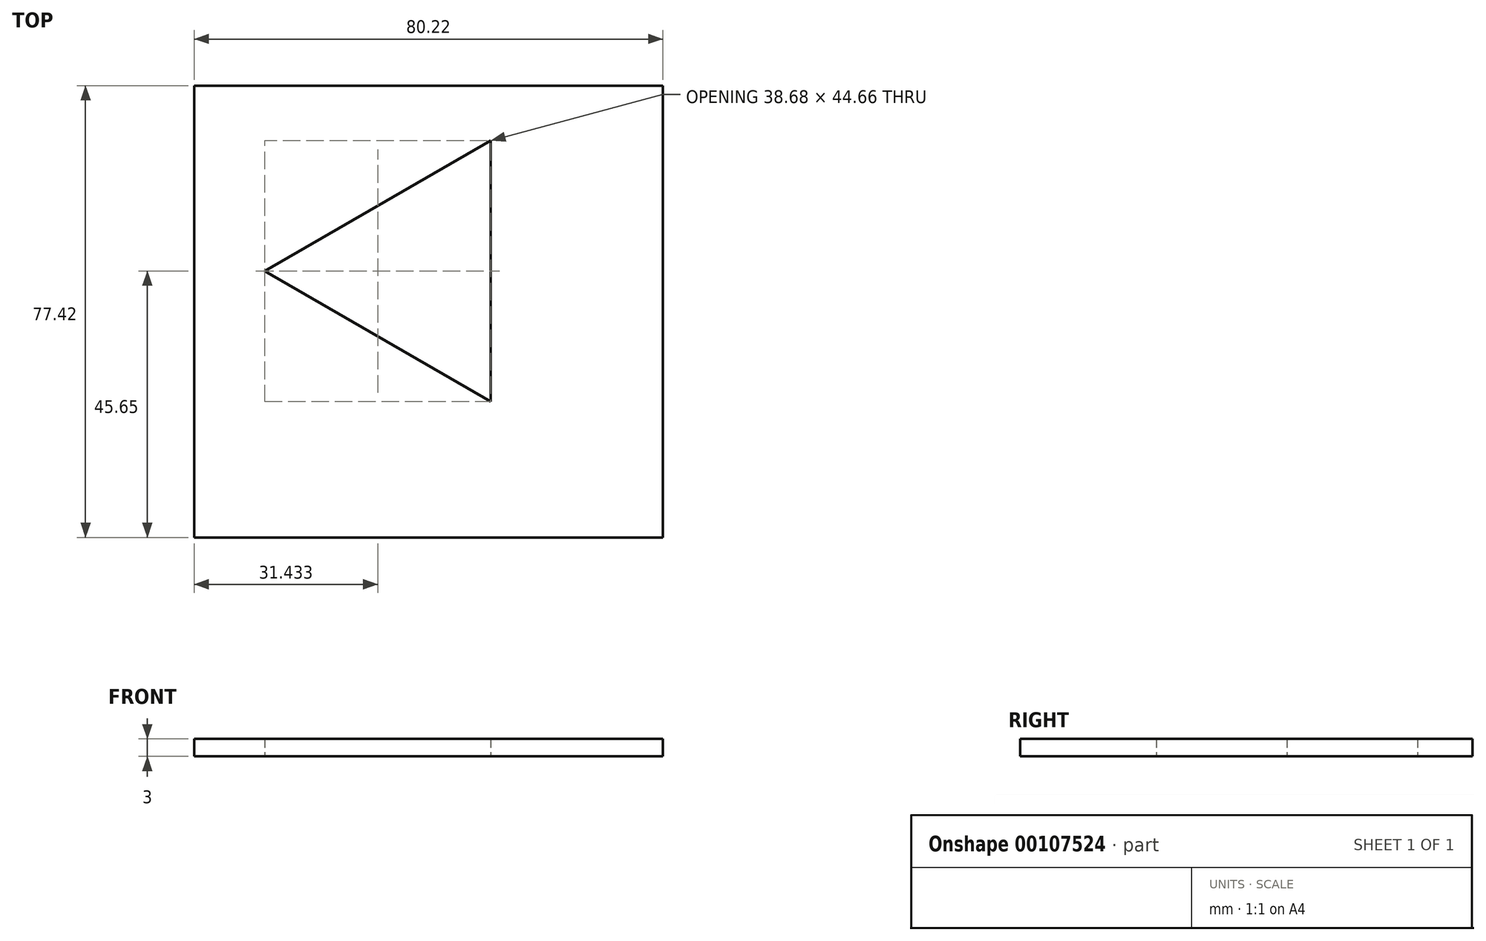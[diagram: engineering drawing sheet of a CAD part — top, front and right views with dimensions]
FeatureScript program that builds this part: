
annotation { "Feature Type Name" : "Feature", "Feature Type Description" : "" }
export const myFeature = defineFeature(function(context is Context, id is Id, definition is map)
    precondition{}
    {
        {
            var Q0;
            Q0=qCreatedBy(makeId("Top.planeOp"),FACE);
            var sketch = newSketch(context, id + "F0", { "sketchPlane" : qUnion([Q0])});
            skLineSegment(sketch, "E0.bottom", {"start": v(-67.86, -45.65) * mm, "end": v(12.36, -45.65) * mm});
            skLineSegment(sketch, "E0.top", {"start": v(-67.86, 31.77) * mm, "end": v(12.36, 31.77) * mm});
            skLineSegment(sketch, "E0.left", {"start": v(-67.86, -45.65) * mm, "end": v(-67.86, 31.77) * mm});
            skLineSegment(sketch, "E0.right", {"start": v(12.36, -45.65) * mm, "end": v(12.36, 31.77) * mm});
            skCircle(sketch, "E1.cCircle", {"center": v(-29.98, 0) * mm, "radius": 12.9 * mm, "construction": true});
            skLineSegment(sketch, "E1.0", {"start": v(-17.09, 22.33) * mm, "end": v(-17.09, -22.33) * mm});
            skLineSegment(sketch, "E1.1", {"start": v(-17.09, -22.33) * mm, "end": v(-55.77, 0) * mm});
            skLineSegment(sketch, "E1.2", {"start": v(-55.77, 0) * mm, "end": v(-17.09, 22.33) * mm});
            skPoint(sketch, "E1.0.midPoint", {"position": v(-17.09, 0) * mm});
            skSolve(sketch);
        }
        {
            var Q0;
            Q0 = qSketchRegion(id + "F0", true);
            extrude(context, id + "F1", {"entities" : qUnion([Q0]), "depth" : 3 * mm});
        }
    });
